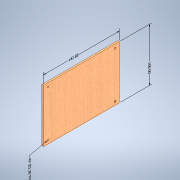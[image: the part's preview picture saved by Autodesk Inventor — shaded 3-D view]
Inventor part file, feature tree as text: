
AUTODESK INVENTOR PART (.ipt)
format: ipt  version: 2022 (Build 260153000, 153)  size: 141,312 bytes
history: native  units: mm
features: other x4, extrude x2, sketch x2, hole x1
ambient origin geometry x8: Origin, YZ Plane, XZ Plane, XY Plane, X Axis, Y Axis, Z Axis, Center Point
bodies: Solid1 (feature_tree)
feature tree (9):
  other  "Vertical_Plate"
  other  "Annotations"
  extrude  "Side_Base"  Depth=100.0mm
  extrude  "Joint_Holes"  Depth=100.0mm
  sketch  "Sketch1"  dims[d0=142.85mm d1=100.0mm]
  sketch  "Sketch2"  dims[d2=3.175mm d3=0.0mm d4=3.3mm d5=6.6mm d6=8.15mm d8=6.6mm d9=0.0mm d10=0.0mm d19=126.48mm d20=8.22mm d11=5.203611mm d12=3.356478mm d13=142.85mm d14=9.218915mm d15=1.439094mm d16=100.0mm d17=20.548853mm]
  other  "Linear Dimension 1"
  other  "Linear Dimension 2"
  hole  "Hole Note 1"  [1 undecoded]
note: 1 required parameter value undecoded (feature->parameter linkage not recoverable at this tier; creation-order binding heuristic only, values carry confidence <= 0.55)
